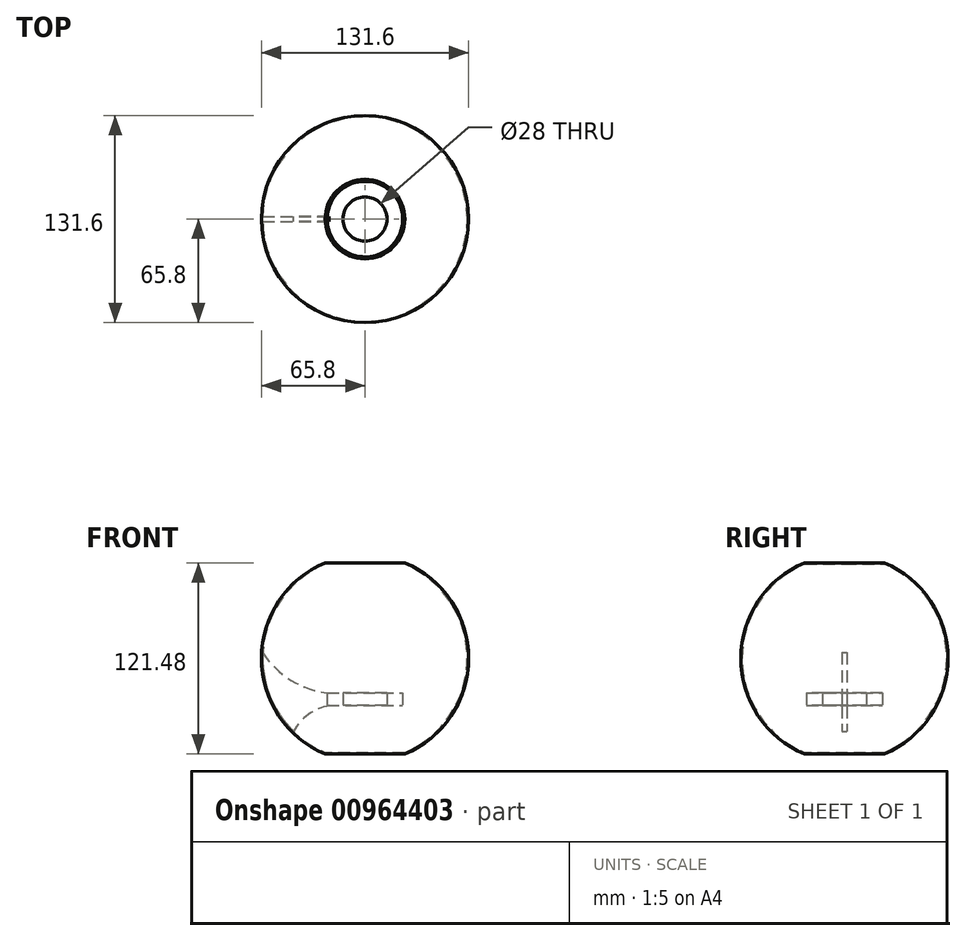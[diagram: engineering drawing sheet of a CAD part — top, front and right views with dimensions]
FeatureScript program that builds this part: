
annotation { "Feature Type Name" : "Feature", "Feature Type Description" : "" }
export const myFeature = defineFeature(function(context is Context, id is Id, definition is map)
    precondition{}
    {
        {
            var Q0;
            Q0=qCreatedBy(makeId("Top.planeOp"),FACE);
            var sketch = newSketch(context, id + "F0", { "sketchPlane" : qUnion([Q0])});
            skCircle(sketch, "E0", {"center": v(0, 0) * mm, "radius": 14 * mm});
            skCircle(sketch, "E1", {"center": v(0, 0) * mm, "radius": 24 * mm});
            skSolve(sketch);
        }
        {
            var Q0;
            Q0 = qSketchRegion(id + "F0", true);
            extrude(context, id + "F1", {"entities" : qUnion([Q0]), "depth" : 8 * mm, "offsetDistance" : 25 * mm});
        }
        {
            var Q0;
            Q0=qCreatedBy(makeId("Front.planeOp"),FACE);
            var sketch = newSketch(context, id + "F2", { "sketchPlane" : qUnion([Q0])});
            skLineSegment(sketch, "E2", {"start": v(-22.72, 0) * mm, "end": v(-22.72, 8) * mm});
            skPoint(sketch, "E3.startSnap0", {"position": v(-22.72, 4) * mm});
            skLineSegment(sketch, "E4", {"start": v(0, 30) * mm, "end": v(0, 0) * mm, "construction": true});
            skArc(sketch, "E5", {"start": v(-64.9, 33.77) * mm, "mid": v(-60.63, 6.56) * mm, "end": v(-45.48, -16.44) * mm});
            skLineSegment(sketch, "E6.bottom", {"start": v(-25, 90) * mm, "end": v(25, 90) * mm, "construction": true});
            skLineSegment(sketch, "E6.top", {"start": v(-25, -30) * mm, "end": v(25, -30) * mm, "construction": true});
            skLineSegment(sketch, "E6.left", {"start": v(-25, 90) * mm, "end": v(-25, -30) * mm, "construction": true});
            skLineSegment(sketch, "E6.right", {"start": v(25, 90) * mm, "end": v(25, -30) * mm, "construction": true});
            skLineSegment(sketch, "E7", {"start": v(0, 0) * mm, "end": v(0, -30) * mm, "construction": true});
            skArc(sketch, "E8.trimOffspring", {"start": v(25, -30) * mm, "mid": v(65, 30) * mm, "end": v(25, 90) * mm, "construction": true});
            skArc(sketch, "E9", {"start": v(-64.9, 33.77) * mm, "mid": v(-46.8, 16) * mm, "end": v(-22.72, 8) * mm});
            skArc(sketch, "E10", {"start": v(-22.72, 0) * mm, "mid": v(-35.9, -5.72) * mm, "end": v(-45.48, -16.44) * mm});
            skLineSegment(sketch, "E11", {"start": v(-24, 0) * mm, "end": v(-24, 8) * mm, "construction": true});
            skSolve(sketch);
        }
        {
            var Q0;
            Q0=makeQuery(id+"F2.imprint","IMPRINT",FACE,{"disambiguationData":[TD([[makeQuery(id+"F2.imprint","IMPRINT",EDGE,{"derivedFrom":sQuery(id+"F2.wireOp",EDGE,"E2")}),1.0]])]});
            extrude(context, id + "F3", {"entities" : qUnion([Q0]), "operationType" : NewBodyOperationType.ADD, "endBound" : BoundingType.SYMMETRIC, "depth" : 3 * mm, "offsetDistance" : 25 * mm});
        }
        {
            var Q0;
            Q0=qCreatedBy(makeId("Front.planeOp"),FACE);
            var sketch = newSketch(context, id + "F4", { "sketchPlane" : qUnion([Q0])});
            skArc(sketch, "E12.0", {"start": v(25, -30) * mm, "mid": v(65, 30) * mm, "end": v(25, 90) * mm});
            skArc(sketch, "E13.0", {"start": v(25.3, -30.74) * mm, "mid": v(65.8, 30) * mm, "end": v(25.3, 90.74) * mm});
            skLineSegment(sketch, "E14", {"start": v(25.3, 90.74) * mm, "end": v(25, 90) * mm});
            skLineSegment(sketch, "E15", {"start": v(25, -30) * mm, "end": v(25.3, -30.74) * mm});
            skSolve(sketch);
        }
        {
            var Q0;
            Q0 = qSketchRegion(id + "F4", true);
            var Q1;
            Q1=sQuery(id+"F2.wireOp",EDGE,"E4");
            revolve(context, id + "F5", {"surfaceOperationType" : NewSurfaceOperationType.NEW, "entities" : qUnion([Q0]), "axis" : qUnion([Q1]), "revolveType" : RevolveType.FULL});
        }
    });
